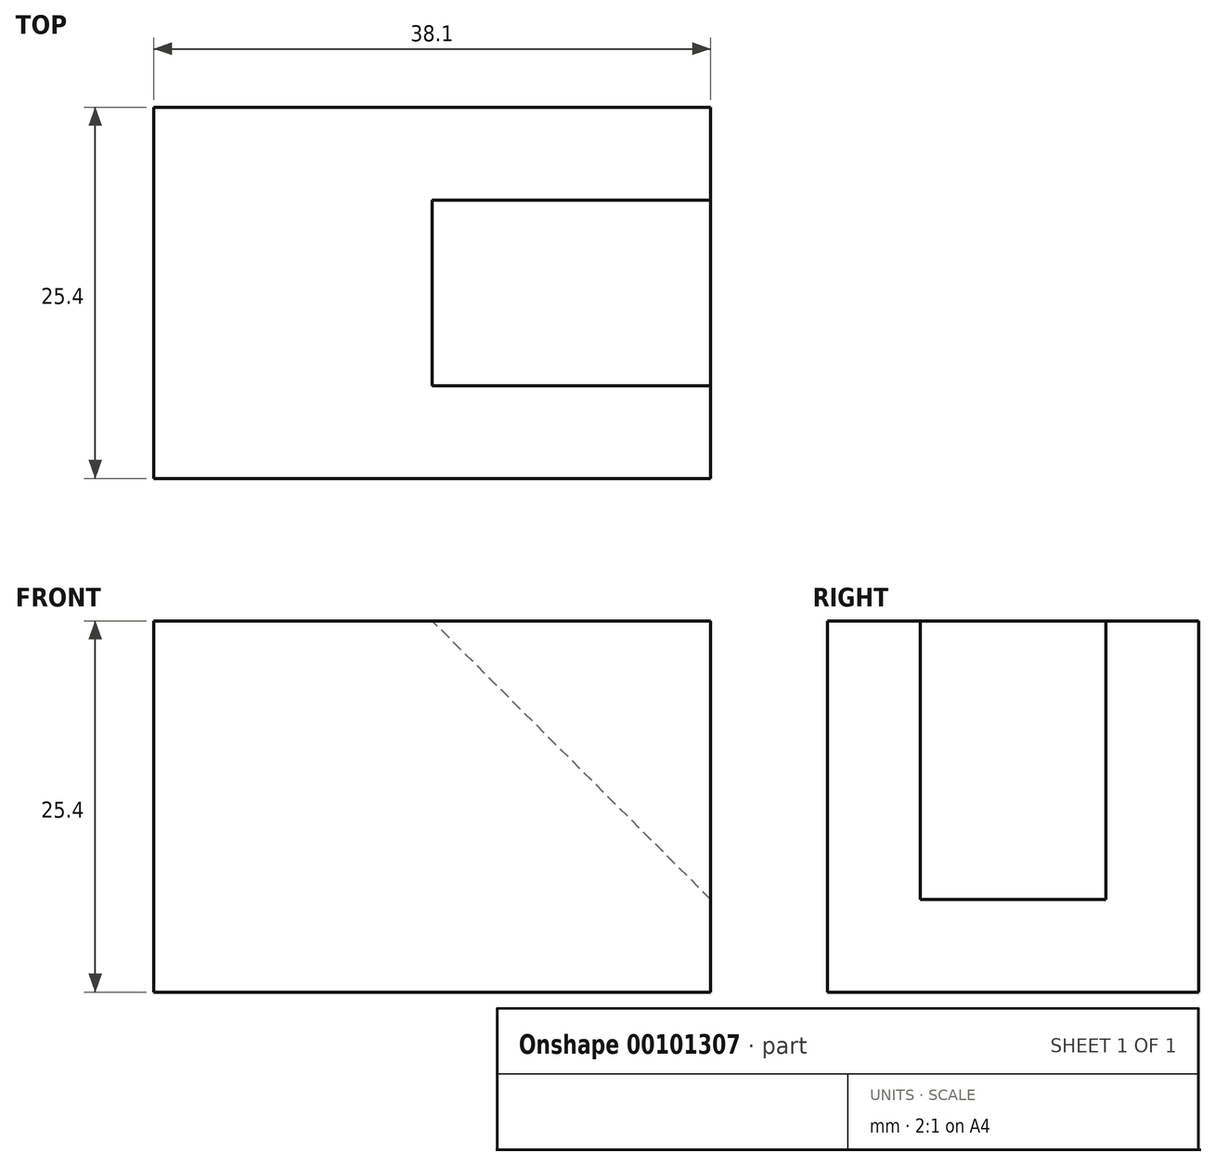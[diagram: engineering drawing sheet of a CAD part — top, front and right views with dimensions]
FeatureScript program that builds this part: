
annotation { "Feature Type Name" : "Feature", "Feature Type Description" : "" }
export const myFeature = defineFeature(function(context is Context, id is Id, definition is map)
    precondition{}
    {
        {
            var Q0;
            Q0=qCreatedBy(makeId("Front.planeOp"),FACE);
            var sketch = newSketch(context, id + "F0", { "sketchPlane" : qUnion([Q0])});
            skLineSegment(sketch, "E0", {"start": v(0, 0) * mm, "end": v(-38.1, 0) * mm});
            skLineSegment(sketch, "E1", {"start": v(-38.1, 0) * mm, "end": v(-38.1, 25.4) * mm});
            skLineSegment(sketch, "E2", {"start": v(-38.1, 25.4) * mm, "end": v(0, 25.4) * mm});
            skLineSegment(sketch, "E3", {"start": v(0, 25.4) * mm, "end": v(0, 0) * mm});
            skLineSegment(sketch, "E4", {"start": v(0, 6.35) * mm, "end": v(-19.05, 25.4) * mm});
            skSolve(sketch);
        }
        {
            var Q0;
            Q0 = qSketchRegion(id + "F0", true);
            extrude(context, id + "F1", {"entities" : qUnion([Q0]), "endBound" : BoundingType.SYMMETRIC, "depth" : 25.4 * mm});
        }
        {
            var Q0;
            {var subQ3=sQuery(id+"F0.wireOp",EDGE,"E4");Q0=makeQuery(id+"F0.imprint","IMPRINT",FACE,{"disambiguationData":[TD([[makeQuery(id+"F0.imprint","IMPRINT",EDGE,{"derivedFrom":subQ3}),-1.0]])]});}
            extrude(context, id + "F2", {"entities" : qUnion([Q0]), "operationType" : NewBodyOperationType.REMOVE, "endBound" : BoundingType.SYMMETRIC, "depth" : 12.7 * mm});
        }
    });
